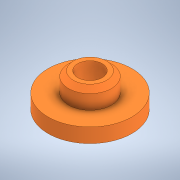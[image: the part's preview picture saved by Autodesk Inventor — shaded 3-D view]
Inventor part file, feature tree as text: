
AUTODESK INVENTOR PART (.ipt)
format: ipt  version: 2022 (Build 260153000, 153)  size: 129,024 bytes
history: native  units: mm
features: extrude x2, sketch x2, chamfer x1
ambient origin geometry x8: Origin, YZ Plane, XZ Plane, XY Plane, X Axis, Y Axis, Z Axis, Center Point
bodies: Solid1 (feature_tree)
feature tree (5):
  extrude  "Extrusion1"  Depth=8.0mm
  chamfer  "Chamfer1"  Distance=8.0mm
  extrude  "Extrusion2"  Depth=6.0mm
  sketch  "Sketch1"  dims[d0=10.2mm d1=17.9mm d2=8.0mm d3=0.0mm]
  sketch  "Sketch2"  dims[d4=2.0mm d5=2.0mm d6=45.0deg d7=35.0mm d8=6.0mm d9=0.0mm]
